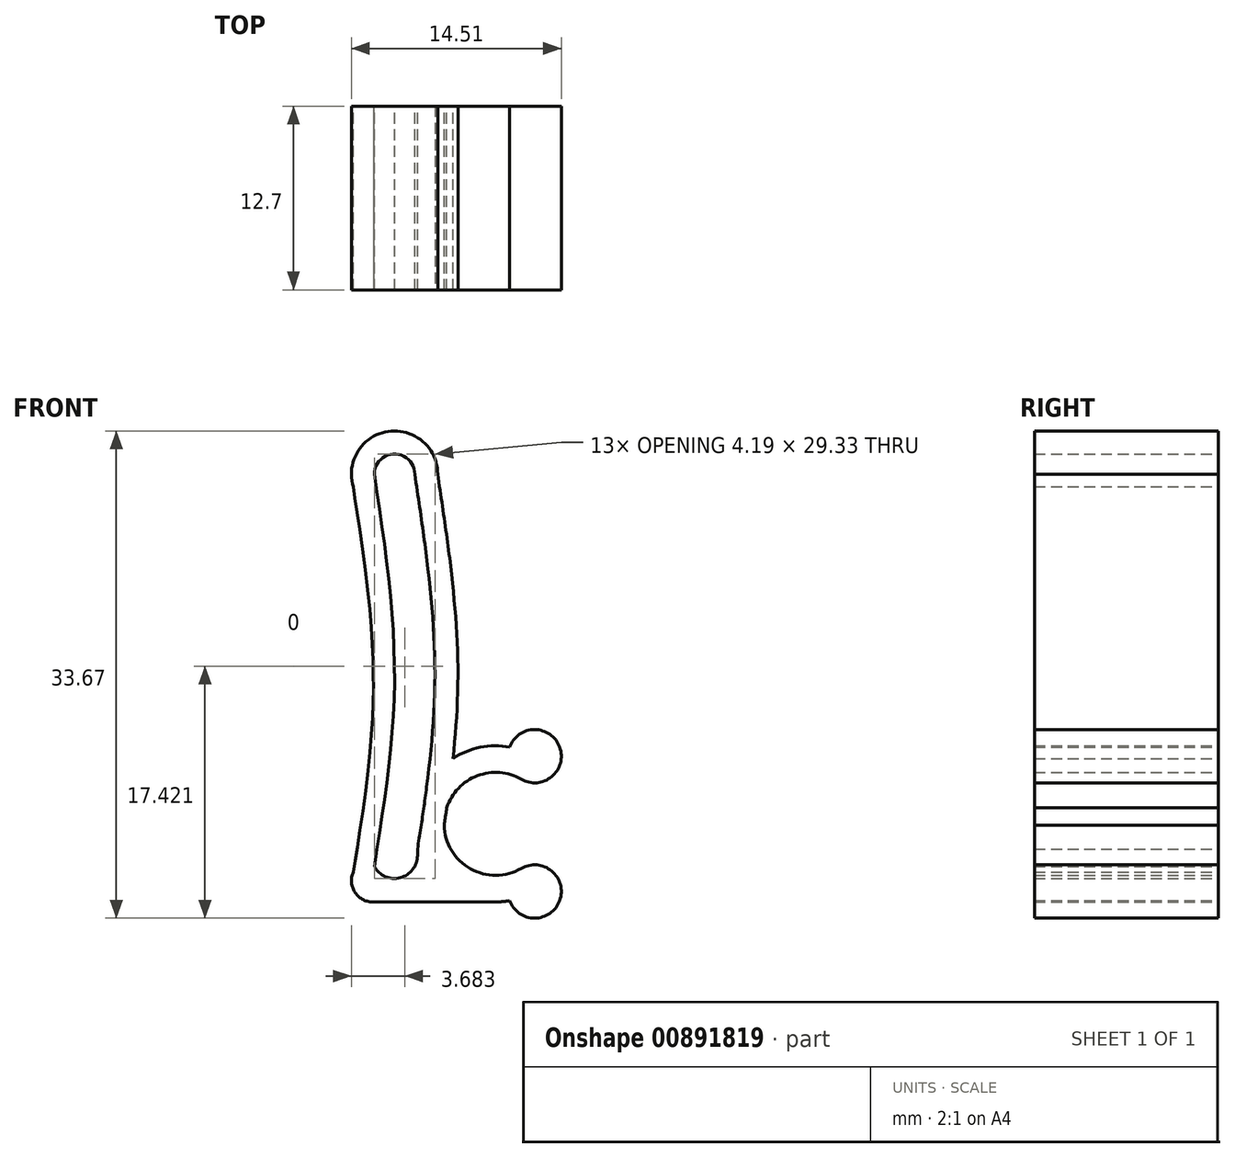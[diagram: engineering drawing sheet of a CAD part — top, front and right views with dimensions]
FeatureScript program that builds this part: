
annotation { "Feature Type Name" : "Feature", "Feature Type Description" : "" }
export const myFeature = defineFeature(function(context is Context, id is Id, definition is map)
    precondition{}
    {
        {
            var Q0;
            Q0=qCreatedBy(makeId("Front.planeOp"),FACE);
            var sketch = newSketch(context, id + "F0", { "sketchPlane" : qUnion([Q0])});
            skArc(sketch, "E0.0", {"start": v(0, -5.4) * mm, "mid": v(0.49, -5.38) * mm, "end": v(0.97, -5.3) * mm});
            skLineSegment(sketch, "E1", {"start": v(0, -5.4) * mm, "end": v(-8.57, -5.4) * mm});
            skLineSegment(sketch, "E2", {"start": v(-6.99, -3.77) * mm, "end": v(-6.98, -3.77) * mm});
            skArc(sketch, "E3.filletArc", {"start": v(-8.38, -2.94) * mm, "mid": v(-7.8, -3.55) * mm, "end": v(-6.99, -3.77) * mm});
            skLineSegment(sketch, "E4", {"start": v(-5.4, 0) * mm, "end": v(-5.4, -2.18) * mm});
            skArc(sketch, "E5.filletArc", {"start": v(-6.98, -3.77) * mm, "mid": v(-5.86, -3.3) * mm, "end": v(-5.4, -2.18) * mm});
            skArc(sketch, "E6.trimOffspring", {"start": v(0.97, 5.3) * mm, "mid": v(-3.46, 4.15) * mm, "end": v(-5.4, 0) * mm});
            skFitSpline(sketch, "E7", {"points": [v(-8.38, -2.94) * mm, v(-6.99, 10.2) * mm, v(-8.38, 24.17) * mm], "startDerivative": vector(4.21, 26.47) * mm, "endDerivative": vector(-4.17, 27.74) * mm});
            skArc(sketch, "E8", {"start": v(-5.59, 24.17) * mm, "mid": v(-6.99, 25.57) * mm, "end": v(-8.38, 24.17) * mm});
            skArc(sketch, "E9.0", {"start": v(-4, 24.17) * mm, "mid": v(-7.43, 27.12) * mm, "end": v(-9.84, 23.3) * mm});
            skFitSpline(sketch, "E10.0", {"points": [v(-9.84, -3.33) * mm, v(-9.66, -2.23) * mm, v(-9.31, -0.03) * mm, v(-8.86, 3.24) * mm, v(-8.6, 5.96) * mm, v(-8.48, 8.13) * mm, v(-8.45, 9.76) * mm, v(-8.48, 11.4) * mm, v(-8.6, 13.62) * mm, v(-8.87, 16.42) * mm, v(-9.32, 19.83) * mm, v(-9.66, 22.14) * mm, v(-9.84, 23.3) * mm]});
            skArc(sketch, "E11.trimOffspring", {"start": v(-9.84, -3.33) * mm, "mid": v(-9.7, -4.76) * mm, "end": v(-8.41, -5.4) * mm});
            skArc(sketch, "E12", {"start": v(-4.68, 17.63) * mm, "mid": v(-3.81, 17.03) * mm, "end": v(-3.11, 17.82) * mm});
            skPoint(sketch, "E13.orphan", {"position": v(-3.11, 17.82) * mm});
            skFitSpline(sketch, "E14.trimOffspring", {"points": [v(-4, -2.94) * mm, v(-2.6, 10.2) * mm, v(-4, 24.17) * mm], "startDerivative": vector(4.21, 26.47) * mm, "endDerivative": vector(-4.17, 27.74) * mm});
            skFitSpline(sketch, "E15.trimOffspring", {"points": [v(-5.59, -2.94) * mm, v(-4.2, 10.2) * mm, v(-5.59, 24.17) * mm], "startDerivative": vector(4.21, 26.47) * mm, "endDerivative": vector(-4.17, 27.74) * mm});
            skArc(sketch, "E16", {"start": v(1.78, 3.08) * mm, "mid": v(-3.56, 0) * mm, "end": v(1.78, -3.08) * mm});
            skArc(sketch, "E17", {"start": v(0.97, -5.3) * mm, "mid": v(4.43, -5.3) * mm, "end": v(1.78, -3.08) * mm});
            skArc(sketch, "E18.MirrorC", {"start": v(0.97, 5.3) * mm, "mid": v(4.43, 5.3) * mm, "end": v(1.78, 3.08) * mm});
            skSolve(sketch);
        }
        {
            var Q0;
            Q0 = qSketchRegion(id + "F0", true);
            extrude(context, id + "F1", {"entities" : qUnion([Q0]), "endBound" : BoundingType.SYMMETRIC, "depth" : 12.7 * mm, "offsetDistance" : 25.4 * mm});
        }
    });
